# Revit family: Турникет трипод PERCo_TTR-10
name_source: partatom
category: Mechanical Equipment
units: mm (PartAtom-declared; Revit-internal decimal feet)

## family parameters
Always vertical = No
Classification = None
Cut with Voids When Loaded = No
Part Type = Normal
Room Calculation Point = No
Round Connector Dimension = Use Diameter
Shared = No
Work Plane-Based = No

## types (2) — shared parameters
Built-in reader = not provided
Colour = stainless steel
Current = 6 A
Electrical connection = 220 B
Floor mount_coating = Panel
Floor mount_frame = Stainless steel
Frame = Stainless steel
IP Code = IP54
Manufacturer = PERCo
Material = Housing, barrier arms ─ high-quality stainless steel.
Maximum dimensions of ACS controller = not provided
Maximum dimensions of installed readers = not provided
Number = 1
Operating temperature = from -40°С to +50°С
Passageway width = 500 mm
Plank base = Black
Plank length = 539 mm  [stored 1.76837 ft]
Planks = Stainless steel
Rated power = 150 W
Throughput rate = 30 persons/min
URL = https://www.perco.com
Unit of measurement = pcs
Voltage = 24 V

## per-type parameters (varying)
| type | Dimensions | Floor mount | Full name | Name | Weight |
| TTR-10AB | 1055×800×760 mm | Yes | TTR-10АB Motorized Tripod Turnstile with Automatic Anti-Panic Barrier Arms for outdoor application | TTR-10АB Tripod Turnstile | max 33 kg |
| TTR-10AK | 613×800×714 mm | No | TTR-10АK All-weather motorized turnstile with automatic anti-panic arms | TTR-10АK Turnstile | max 55 kg |

note: [stored X ft] marks values corroborated as IEEE doubles in the binary element streams (Revit-internal decimal feet)
